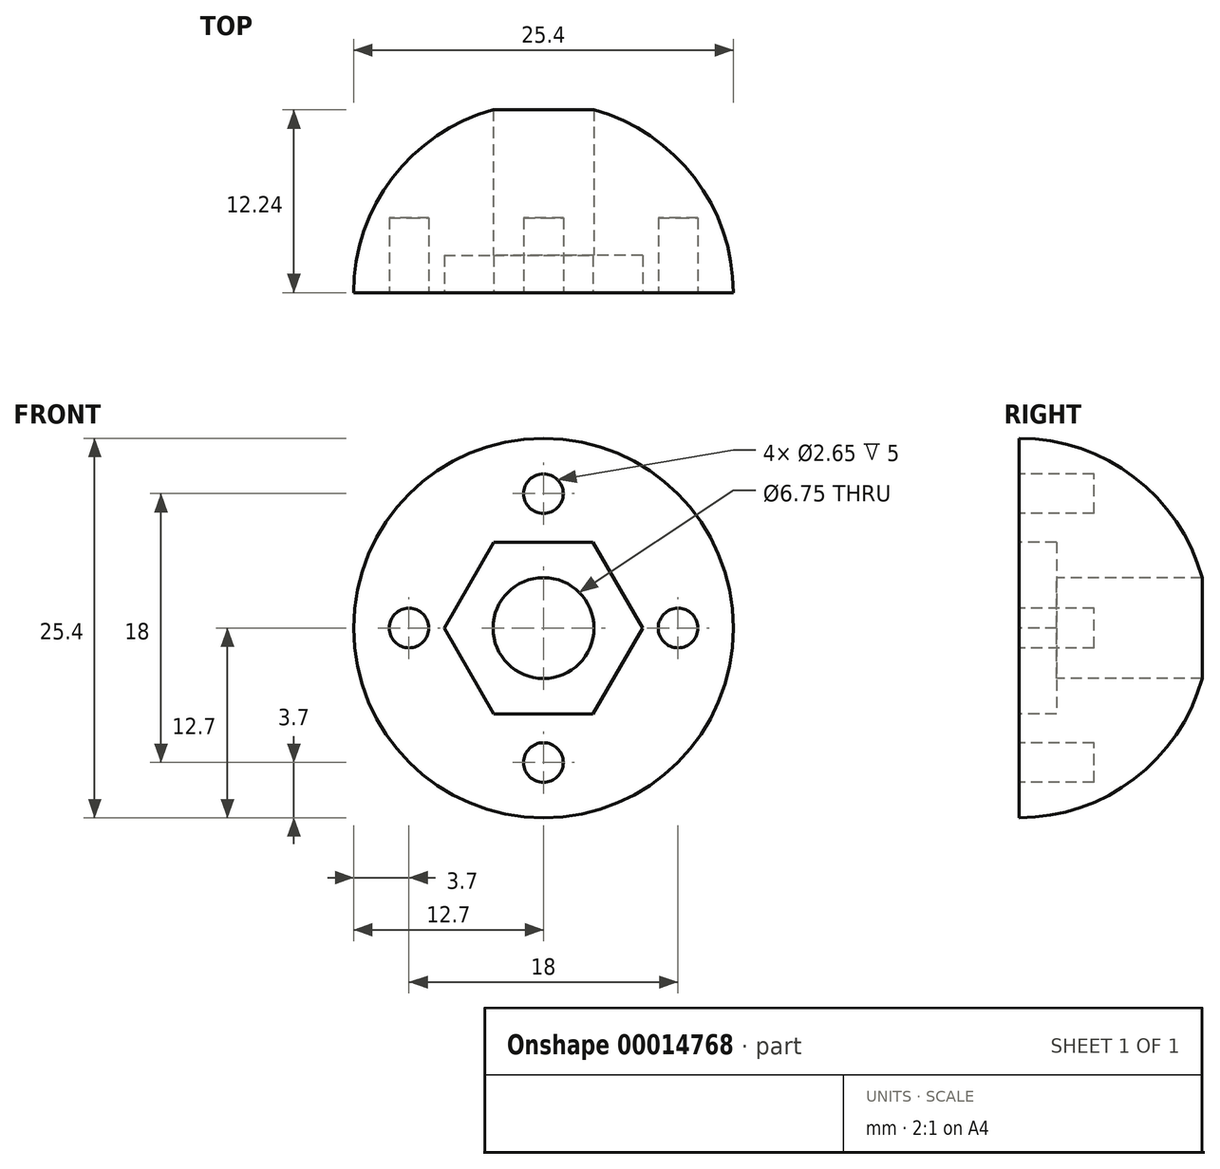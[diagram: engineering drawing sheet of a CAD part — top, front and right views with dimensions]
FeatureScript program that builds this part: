
annotation { "Feature Type Name" : "Feature", "Feature Type Description" : "" }
export const myFeature = defineFeature(function(context is Context, id is Id, definition is map)
    precondition{}
    {
        {
            var Q0;
            Q0=qCreatedBy(makeId("Top.planeOp"),FACE);
            var sketch = newSketch(context, id + "F0", { "sketchPlane" : qUnion([Q0])});
            skArc(sketch, "E0", {"start": v(12.7, 0) * mm, "mid": v(0, 12.7) * mm, "end": v(-12.7, 0) * mm});
            skLineSegment(sketch, "E1", {"start": v(-12.7, 0) * mm, "end": v(12.7, 0) * mm});
            skSolve(sketch);
        }
        {
            var Q0;
            Q0=makeQuery(id+"F0.imprint","IMPRINT",FACE,{"disambiguationData":[TD([[makeQuery(id+"F0.imprint","IMPRINT",EDGE,{"derivedFrom":sQuery(id+"F0.wireOp",EDGE,"E0")}),1.0]])]});
            var Q1;
            Q1=sQuery(id+"F0.wireOp",EDGE,"E1");
            revolve(context, id + "F1", {"entities" : qUnion([Q0]), "axis" : qUnion([Q1]), "revolveType" : RevolveType.TWO_DIRECTIONS, "oppositeDirection" : true, "angle" : 90 * degree, "angleBack" : 270 * degree});
        }
        {
            var Q0;
            Q0=qCreatedBy(makeId("Front.planeOp"),FACE);
            var sketch = newSketch(context, id + "F2", { "sketchPlane" : qUnion([Q0])});
            skCircle(sketch, "E2.cCircle", {"center": v(0, 0) * mm, "radius": 5.75 * mm, "construction": true});
            skLineSegment(sketch, "E2.0", {"start": v(3.32, -5.75) * mm, "end": v(-3.32, -5.75) * mm});
            skLineSegment(sketch, "E2.1", {"start": v(-3.32, -5.75) * mm, "end": v(-6.64, 0) * mm});
            skLineSegment(sketch, "E2.2", {"start": v(-6.64, 0) * mm, "end": v(-3.32, 5.75) * mm});
            skLineSegment(sketch, "E2.3", {"start": v(-3.32, 5.75) * mm, "end": v(3.32, 5.75) * mm});
            skLineSegment(sketch, "E2.4", {"start": v(3.32, 5.75) * mm, "end": v(6.64, 0) * mm});
            skLineSegment(sketch, "E2.5", {"start": v(6.64, 0) * mm, "end": v(3.32, -5.75) * mm});
            skPoint(sketch, "E2.0.midPoint", {"position": v(0, -5.75) * mm});
            skSolve(sketch);
        }
        {
            var Q0;
            Q0=makeQuery(id+"F2.imprint","IMPRINT",FACE,{"disambiguationData":[TD([[makeQuery(id+"F2.imprint","IMPRINT",EDGE,{"derivedFrom":sQuery(id+"F2.wireOp",EDGE,"E2.0")}),-1.0]])]});
            extrude(context, id + "F3", {"entities" : qUnion([Q0]), "operationType" : NewBodyOperationType.REMOVE, "oppositeDirection" : true, "depth" : 2.5 * mm});
        }
        {
            var Q0;
            Q0=qCreatedBy(makeId("Front.planeOp"),FACE);
            var sketch = newSketch(context, id + "F4", { "sketchPlane" : qUnion([Q0])});
            skCircle(sketch, "E3", {"center": v(0, 9) * mm, "radius": 1.32 * mm});
            skCircle(sketch, "E4", {"center": v(9, 0) * mm, "radius": 1.32 * mm});
            skCircle(sketch, "E5", {"center": v(0, -9) * mm, "radius": 1.32 * mm});
            skCircle(sketch, "E6", {"center": v(-9, 0) * mm, "radius": 1.32 * mm});
            skSolve(sketch);
        }
        {
            var Q0;
            Q0=qCreatedBy(makeId("Front.planeOp"),FACE);
            var sketch = newSketch(context, id + "F5", { "sketchPlane" : qUnion([Q0])});
            skCircle(sketch, "E7", {"center": v(0, 0) * mm, "radius": 3.38 * mm});
            skSolve(sketch);
        }
        {
            var Q0;
            Q0=makeQuery(id+"F5.imprint","IMPRINT",FACE,{"disambiguationData":[TD([[makeQuery(id+"F5.imprint","IMPRINT",EDGE,{"derivedFrom":sQuery(id+"F5.wireOp",EDGE,"E7")}),1.0]])]});
            extrude(context, id + "F6", {"entities" : qUnion([Q0]), "operationType" : NewBodyOperationType.REMOVE, "endBound" : BoundingType.THROUGH_ALL, "oppositeDirection" : true, "depth" : 25 * mm});
        }
        {
            var Q0;
            Q0=makeQuery(id+"F4.imprint","IMPRINT",FACE,{"disambiguationData":[TD([[makeQuery(id+"F4.imprint","IMPRINT",EDGE,{"derivedFrom":sQuery(id+"F4.wireOp",EDGE,"E6")}),1.0]])]});
            var Q1;
            Q1=makeQuery(id+"F4.imprint","IMPRINT",FACE,{"disambiguationData":[TD([[makeQuery(id+"F4.imprint","IMPRINT",EDGE,{"derivedFrom":sQuery(id+"F4.wireOp",EDGE,"E3")}),1.0]])]});
            var Q2;
            Q2=makeQuery(id+"F4.imprint","IMPRINT",FACE,{"disambiguationData":[TD([[makeQuery(id+"F4.imprint","IMPRINT",EDGE,{"derivedFrom":sQuery(id+"F4.wireOp",EDGE,"E4")}),1.0]])]});
            var Q3;
            Q3=makeQuery(id+"F4.imprint","IMPRINT",FACE,{"disambiguationData":[TD([[makeQuery(id+"F4.imprint","IMPRINT",EDGE,{"derivedFrom":sQuery(id+"F4.wireOp",EDGE,"E5")}),1.0]])]});
            extrude(context, id + "F7", {"entities" : qUnion([Q0, Q1, Q2, Q3]), "operationType" : NewBodyOperationType.REMOVE, "oppositeDirection" : true, "depth" : 5 * mm});
        }
    });
